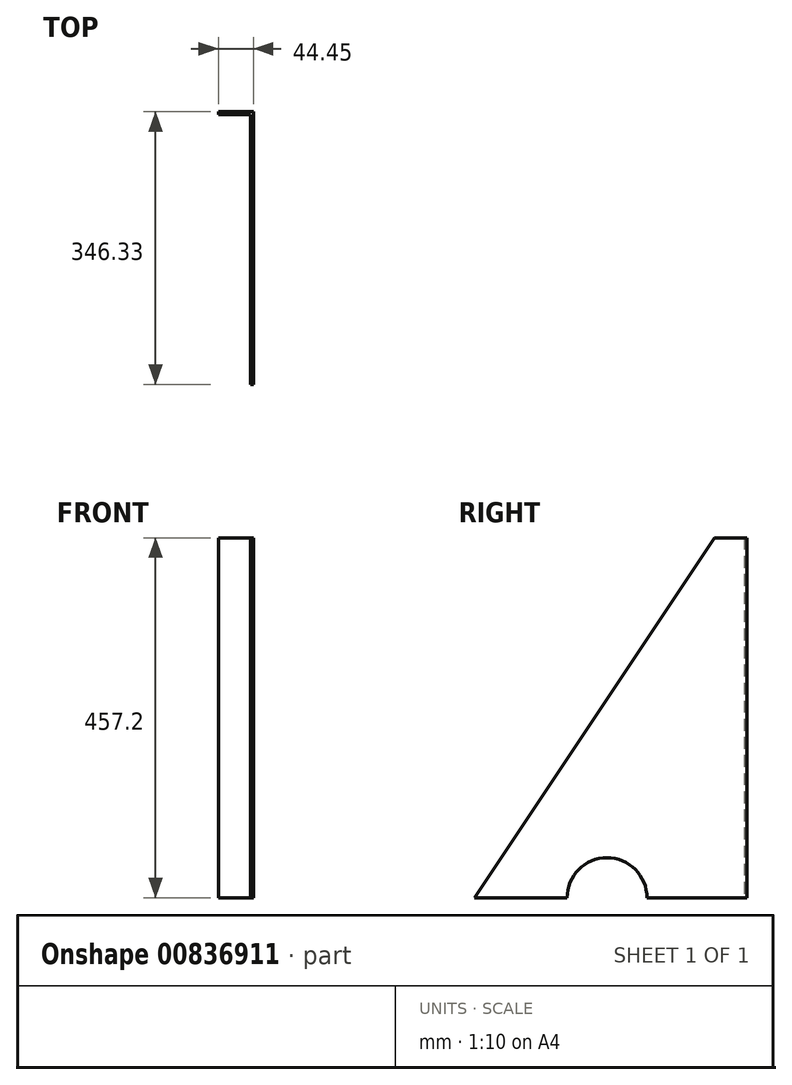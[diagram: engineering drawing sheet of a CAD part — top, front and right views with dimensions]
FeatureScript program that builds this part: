
annotation { "Feature Type Name" : "Feature", "Feature Type Description" : "" }
export const myFeature = defineFeature(function(context is Context, id is Id, definition is map)
    precondition{}
    {
        {
            var Q0;
            Q0=qCreatedBy(makeId("Right.planeOp"),FACE);
            var sketch = newSketch(context, id + "F0", { "sketchPlane" : qUnion([Q0])});
            skLineSegment(sketch, "E0", {"start": v(0, 0) * mm, "end": v(0, 457.2) * mm});
            skLineSegment(sketch, "E1", {"start": v(0, 457.2) * mm, "end": v(-304.8, 0) * mm});
            skLineSegment(sketch, "E2", {"start": v(-304.8, 0) * mm, "end": v(0, 0) * mm});
            skSolve(sketch);
        }
        {
            var Q0;
            Q0 = qSketchRegion(id + "F0", true);
            extrude(context, id + "F1", {"entities" : qUnion([Q0]), "depth" : 3.43 * mm, "offsetDistance" : 25.4 * mm});
        }
        {
            var Q0;
            Q0=qCreatedBy(makeId("Top.planeOp"),FACE);
            var sketch = newSketch(context, id + "F2", { "sketchPlane" : qUnion([Q0])});
            skLineSegment(sketch, "E3", {"start": v(0, 0) * mm, "end": v(0, 38.1) * mm});
            skLineSegment(sketch, "E4", {"start": v(-41.02, 41.53) * mm, "end": v(-41.02, 38.1) * mm});
            skLineSegment(sketch, "E5", {"start": v(3.43, 41.53) * mm, "end": v(-41.02, 41.53) * mm});
            skLineSegment(sketch, "E6", {"start": v(3.43, 41.53) * mm, "end": v(3.43, 0) * mm});
            skLineSegment(sketch, "E7", {"start": v(3.43, 0) * mm, "end": v(0, 0) * mm});
            skLineSegment(sketch, "E8", {"start": v(-41.02, 38.1) * mm, "end": v(0, 38.1) * mm});
            skSolve(sketch);
        }
        {
            var Q0;
            Q0=makeQuery(id+"F2.imprint","IMPRINT",FACE,{"disambiguationData":[TD([[makeQuery(id+"F2.imprint","IMPRINT",EDGE,{"derivedFrom":sQuery(id+"F2.wireOp",EDGE,"E3")}),-1.0]])]});
            var Q1;
            Q1=makeQuery(id+"F1.opExtrude","CAP_VERTEX",VERTEX,{"disambiguationData":[OSD([sQuery(id+"F0.wireOp",EDGE,"E0"),sQuery(id+"F0.wireOp",EDGE,"E1")])],"isStart":true});
            extrude(context, id + "F3", {"entities" : qUnion([Q0]), "operationType" : NewBodyOperationType.ADD, "endBound" : BoundingType.UP_TO_VERTEX, "depth" : 25.4 * mm, "endBoundEntityVertex" : qUnion([Q1]), "offsetDistance" : 25.4 * mm});
        }
        {
            var Q0;
            Q0=makeQuery(id+"F3.boolean.opBoolean","MERGE",FACE,{"derivedFrom":[makeQuery(id+"F1.opExtrude","CAP_FACE",FACE,{"disambiguationData":[OSD([sQuery(id+"F0.wireOp",EDGE,"E0"),sQuery(id+"F0.wireOp",EDGE,"E1"),sQuery(id+"F0.wireOp",EDGE,"E2")])],"isStart":false}),makeQuery(id+"F3.opExtrude","SWEPT_FACE",FACE,{"disambiguationData":[OSD([sQuery(id+"F2.wireOp",EDGE,"E6")])]})]});
            var sketch = newSketch(context, id + "F4", { "sketchPlane" : qUnion([Q0])});
            skCircle(sketch, "E9", {"center": v(-136.27, 0) * mm, "radius": 50.8 * mm});
            skSolve(sketch);
        }
        {
            var Q0;
            Q0 = qSketchRegion(id + "F4", true);
            extrude(context, id + "F5", {"entities" : qUnion([Q0]), "operationType" : NewBodyOperationType.REMOVE, "oppositeDirection" : true, "depth" : 25.4 * mm, "offsetDistance" : 25.4 * mm});
        }
    });
